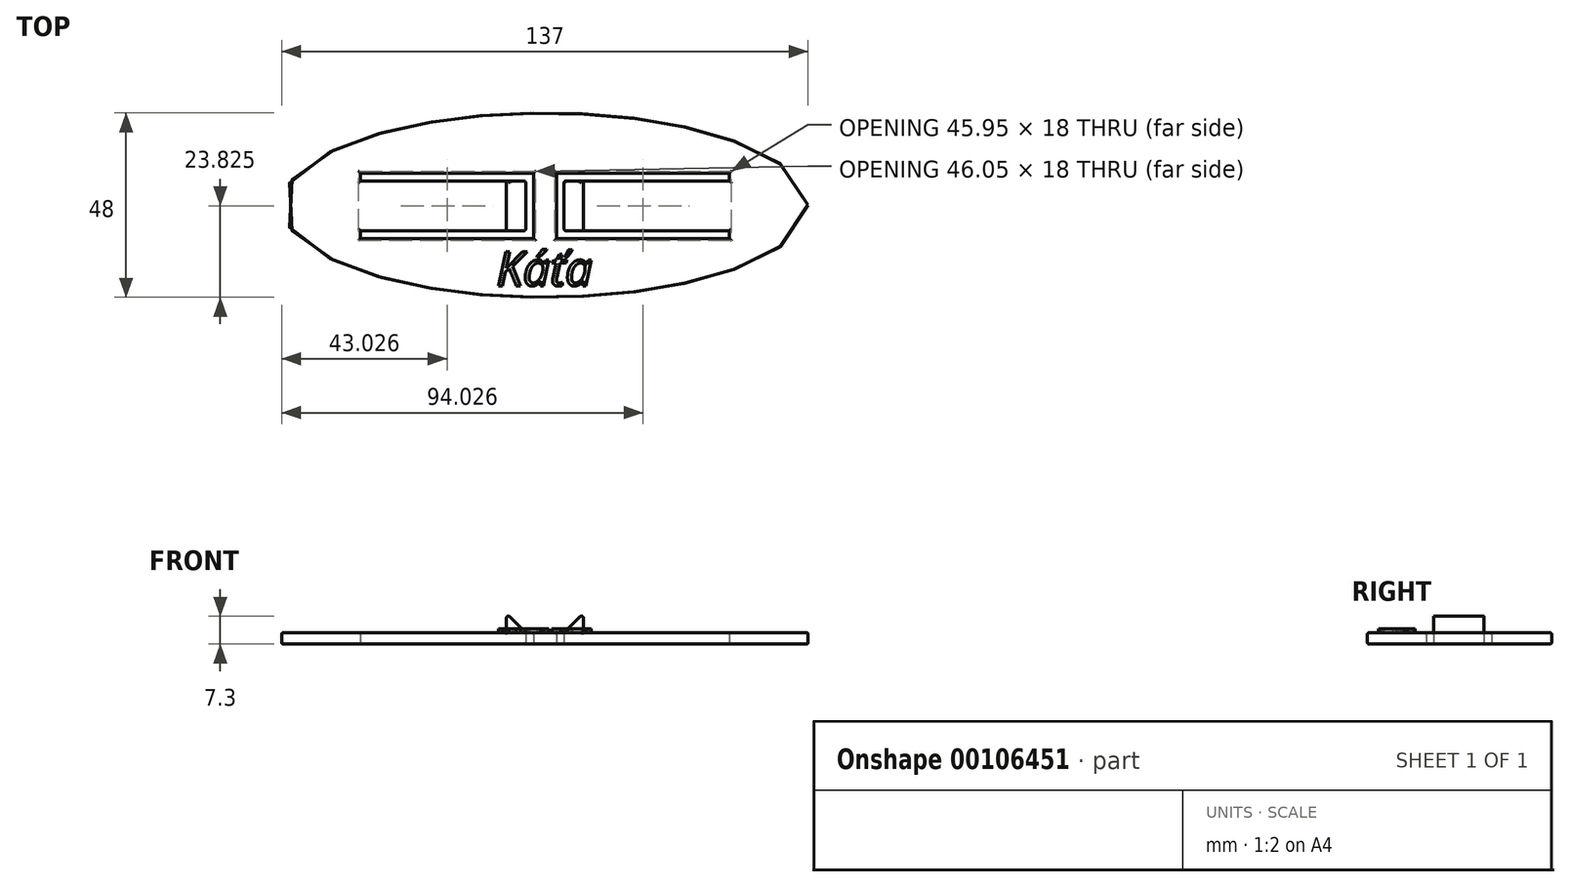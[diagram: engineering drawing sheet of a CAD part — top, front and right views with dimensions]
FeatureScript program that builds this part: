
annotation { "Feature Type Name" : "Feature", "Feature Type Description" : "" }
export const myFeature = defineFeature(function(context is Context, id is Id, definition is map)
    precondition{}
    {
        {
            var Q0;
            Q0=qCreatedBy(makeId("Top.planeOp"),FACE);
            var sketch = newSketch(context, id + "F0", { "sketchPlane" : qUnion([Q0])});
            skEllipse(sketch, "E0", {"center": v(0, 0) * mm, "majorRadius": 68.5 * mm, "minorRadius": 24 * mm, "majorAxis": v(1, 0)});
            skLineSegment(sketch, "E1", {"start": v(-5, -6.67) * mm, "end": v(-48, -6.67) * mm});
            skLineSegment(sketch, "E2", {"start": v(-48, -6.67) * mm, "end": v(-48, -8.67) * mm});
            skLineSegment(sketch, "E3", {"start": v(48, -8.67) * mm, "end": v(48, -6.67) * mm});
            skLineSegment(sketch, "E4", {"start": v(48, -6.67) * mm, "end": v(5, -6.67) * mm});
            skLineSegment(sketch, "E5", {"start": v(5, -6.67) * mm, "end": v(5, 6.33) * mm});
            skLineSegment(sketch, "E6", {"start": v(5, 6.33) * mm, "end": v(48, 6.33) * mm});
            skLineSegment(sketch, "E7", {"start": v(48, 6.33) * mm, "end": v(48, 8.33) * mm});
            skLineSegment(sketch, "E8", {"start": v(-48, 8.33) * mm, "end": v(-48, 6.33) * mm});
            skLineSegment(sketch, "E9", {"start": v(-48, 6.33) * mm, "end": v(-5, 6.33) * mm});
            skLineSegment(sketch, "E10", {"start": v(-5, 6.33) * mm, "end": v(-5, -6.67) * mm});
            skLineSegment(sketch, "E11.left", {"start": v(-2.95, 8.33) * mm, "end": v(-2.95, -8.67) * mm});
            skLineSegment(sketch, "E11.right", {"start": v(3.05, 8.33) * mm, "end": v(3.05, -8.67) * mm});
            skLineSegment(sketch, "E12", {"start": v(-48, -8.67) * mm, "end": v(-2.95, -8.67) * mm});
            skLineSegment(sketch, "E13", {"start": v(3.05, -8.67) * mm, "end": v(48, -8.67) * mm});
            skLineSegment(sketch, "E14", {"start": v(48, 8.33) * mm, "end": v(3.05, 8.33) * mm});
            skLineSegment(sketch, "E15", {"start": v(-2.95, 8.33) * mm, "end": v(-48, 8.33) * mm});
            skLineSegment(sketch, "E16", {"start": v(-70.2, 0) * mm, "end": v(71.44, 0) * mm, "construction": true});
            skPoint(sketch, "E16.endSnap0", {"position": v(68.5, 0) * mm});
            skLineSegment(sketch, "E17", {"start": v(0, -24) * mm, "end": v(71.65, -24) * mm, "construction": true});
            skLineSegment(sketch, "E18", {"start": v(-6.89, -6.67) * mm, "end": v(-6.89, 6.33) * mm, "construction": true});
            skLineSegment(sketch, "E19", {"start": v(7.19, -6.67) * mm, "end": v(7.19, 6.33) * mm, "construction": true});
            skSolve(sketch);
        }
        {
            var Q0;
            Q0=makeQuery(id+"F0.imprint","IMPRINT",FACE,{"disambiguationData":[TD([[makeQuery(id+"F0.imprint","IMPRINT",EDGE,{"derivedFrom":sQuery(id+"F0.wireOp",EDGE,"E0")}),1.0]])]});
            extrude(context, id + "F1", {"entities" : qUnion([Q0]), "endBound" : BoundingType.SYMMETRIC, "depth" : 3 * mm});
        }
        {
            var Q0;
            Q0=makeQuery(id+"F1.opExtrude","CAP_FACE",FACE,{"disambiguationData":[OSD([sQuery(id+"F0.wireOp",EDGE,"E0"),sQuery(id+"F0.wireOp",EDGE,"E1"),sQuery(id+"F0.wireOp",EDGE,"E2"),sQuery(id+"F0.wireOp",EDGE,"E3"),sQuery(id+"F0.wireOp",EDGE,"E4"),sQuery(id+"F0.wireOp",EDGE,"E5"),sQuery(id+"F0.wireOp",EDGE,"E6"),sQuery(id+"F0.wireOp",EDGE,"E7"),sQuery(id+"F0.wireOp",EDGE,"E8"),sQuery(id+"F0.wireOp",EDGE,"E9"),sQuery(id+"F0.wireOp",EDGE,"E10"),sQuery(id+"F0.wireOp",EDGE,"E11.left"),sQuery(id+"F0.wireOp",EDGE,"E11.right"),sQuery(id+"F0.wireOp",EDGE,"E12"),sQuery(id+"F0.wireOp",EDGE,"E13"),sQuery(id+"F0.wireOp",EDGE,"E14"),sQuery(id+"F0.wireOp",EDGE,"E15")])],"isStart":false});
            var sketch = newSketch(context, id + "F2", { "sketchPlane" : qUnion([Q0])});
            skLineSegment(sketch, "E20.bottom", {"start": v(-10, 6.33) * mm, "end": v(-5, 6.33) * mm});
            skLineSegment(sketch, "E20.top", {"start": v(-10, -6.67) * mm, "end": v(-5, -6.67) * mm});
            skLineSegment(sketch, "E20.left", {"start": v(-10, 6.33) * mm, "end": v(-10, -6.67) * mm});
            skLineSegment(sketch, "E20.right", {"start": v(-5, 6.33) * mm, "end": v(-5, -6.67) * mm});
            skLineSegment(sketch, "E21.bottom", {"start": v(5, 6.33) * mm, "end": v(10, 6.33) * mm});
            skLineSegment(sketch, "E21.top", {"start": v(5, -6.67) * mm, "end": v(10, -6.67) * mm});
            skLineSegment(sketch, "E21.left", {"start": v(5, 6.33) * mm, "end": v(5, -6.67) * mm});
            skLineSegment(sketch, "E21.right", {"start": v(10, 6.33) * mm, "end": v(10, -6.67) * mm});
            skSolve(sketch);
        }
        {
            var Q0;
            Q0=makeQuery(id+"F2.imprint","IMPRINT",FACE,{"disambiguationData":[TD([[makeQuery(id+"F2.imprint","IMPRINT",EDGE,{"derivedFrom":sQuery(id+"F2.wireOp",EDGE,"E20.bottom")}),-1.0]])]});
            extrude(context, id + "F3", {"entities" : qUnion([Q0]), "operationType" : NewBodyOperationType.ADD, "depth" : 5 * mm});
        }
        {
            var Q0;
            Q0=makeQuery(id+"F2.imprint","IMPRINT",FACE,{"disambiguationData":[TD([[makeQuery(id+"F2.imprint","IMPRINT",EDGE,{"derivedFrom":sQuery(id+"F2.wireOp",EDGE,"E21.bottom")}),-1.0]])]});
            extrude(context, id + "F4", {"entities" : qUnion([Q0]), "operationType" : NewBodyOperationType.ADD, "depth" : 5 * mm});
        }
        {
            var Q0;
            Q0=makeQuery(id+"F3.boolean.opBoolean","MERGE",FACE,{"derivedFrom":[makeQuery(id+"F1.opExtrude","SWEPT_FACE",FACE,{"disambiguationData":[OSD([sQuery(id+"F0.wireOp",EDGE,"E1")])]}),makeQuery(id+"F3.opExtrude","SWEPT_FACE",FACE,{"disambiguationData":[OSD([sQuery(id+"F2.wireOp",EDGE,"E20.top")])]})]});
            var sketch = newSketch(context, id + "F5", { "sketchPlane" : qUnion([Q0])});
            skLineSegment(sketch, "E22", {"start": v(-5, 1.57) * mm, "end": v(-10, 6.5) * mm});
            skSolve(sketch);
        }
        {
            var Q0;
            {var subQ0=sQuery(id+"F5.wireOp",EDGE,"E22");Q0=makeQuery(id+"F5.imprint","IMPRINT",FACE,{"disambiguationData":[TD([[makeQuery(id+"F5.imprint","IMPRINT",EDGE,{"derivedFrom":subQ0}),-1.0]])]});}
            extrude(context, id + "F6", {"entities" : qUnion([Q0]), "operationType" : NewBodyOperationType.REMOVE, "oppositeDirection" : true, "depth" : 25 * mm});
        }
        {
            var Q0;
            Q0=makeQuery(id+"F4.boolean.opBoolean","MERGE",FACE,{"derivedFrom":[makeQuery(id+"F1.opExtrude","SWEPT_FACE",FACE,{"disambiguationData":[OSD([sQuery(id+"F0.wireOp",EDGE,"E4")])]}),makeQuery(id+"F4.opExtrude","SWEPT_FACE",FACE,{"disambiguationData":[OSD([sQuery(id+"F2.wireOp",EDGE,"E21.top")])]})]});
            var sketch = newSketch(context, id + "F7", { "sketchPlane" : qUnion([Q0])});
            skLineSegment(sketch, "E23", {"start": v(10, 6.5) * mm, "end": v(5, 1.5) * mm});
            skSolve(sketch);
        }
        {
            var Q0;
            {var subQ0=sQuery(id+"F7.wireOp",EDGE,"E23");Q0=makeQuery(id+"F7.imprint","IMPRINT",FACE,{"disambiguationData":[TD([[makeQuery(id+"F7.imprint","IMPRINT",EDGE,{"derivedFrom":subQ0}),-1.0]])]});}
            extrude(context, id + "F8", {"entities" : qUnion([Q0]), "operationType" : NewBodyOperationType.REMOVE, "oppositeDirection" : true, "depth" : 25 * mm});
        }
        {
            var Q0;
            Q0=makeQuery(id+"F1.opExtrude","CAP_EDGE",EDGE,{"disambiguationData":[OSD([sQuery(id+"F0.wireOp",EDGE,"E0")])],"isStart":false});
            var Q1;
            Q1=makeQuery(id+"F1.opExtrude","CAP_EDGE",EDGE,{"disambiguationData":[OSD([sQuery(id+"F0.wireOp",EDGE,"E0")])],"isStart":true});
            var Q2;
            Q2=makeQuery(id+"F1.opExtrude","CAP_EDGE",EDGE,{"disambiguationData":[OSD([sQuery(id+"F0.wireOp",EDGE,"E13")])],"isStart":false});
            var Q3;
            Q3=makeQuery(id+"F1.opExtrude","CAP_EDGE",EDGE,{"disambiguationData":[OSD([sQuery(id+"F0.wireOp",EDGE,"E4")])],"isStart":false});
            var Q4;
            Q4=makeQuery(id+"F1.opExtrude","CAP_EDGE",EDGE,{"disambiguationData":[OSD([sQuery(id+"F0.wireOp",EDGE,"E3")])],"isStart":false});
            var Q5;
            Q5=makeQuery(id+"F8.boolean.opBoolean","COPY",EDGE,{"derivedFrom":makeQuery(id+"F8.opExtrude","CAP_EDGE",EDGE,{"disambiguationData":[OSD([sQuery(id+"F7.wireOp",EDGE,"E23")])],"isStart":true})});
            var Q6;
            Q6=makeQuery(id+"F4.boolean.opBoolean","MERGE",EDGE,{"derivedFrom":[makeQuery(id+"F1.opExtrude","SWEPT_EDGE",EDGE,{"disambiguationData":[OSD([sQuery(id+"F0.wireOp",EDGE,"E4"),sQuery(id+"F0.wireOp",EDGE,"E5")])]}),makeQuery(id+"F4.opExtrude","SWEPT_EDGE",EDGE,{"disambiguationData":[OSD([sQuery(id+"F2.wireOp",EDGE,"E21.top"),sQuery(id+"F2.wireOp",EDGE,"E21.left")])]})]});
            var Q7;
            Q7=makeQuery(id+"F8.boolean.opBoolean","COPY",EDGE,{"derivedFrom":makeQuery(id+"F8.opExtrude","SWEPT_EDGE",EDGE,{"disambiguationData":[OSD([sQuery(id+"F0.wireOp",EDGE,"E4"),sQuery(id+"F0.wireOp",EDGE,"E5"),sQuery(id+"F2.wireOp",EDGE,"E21.top"),sQuery(id+"F2.wireOp",EDGE,"E21.left"),sQuery(id+"F7.wireOp",EDGE,"E23")])]})});
            var Q8;
            Q8=makeQuery(id+"F8.boolean.opBoolean","INTERSECT",EDGE,{"derivedFrom":[makeQuery(id+"F4.boolean.opBoolean","MERGE",FACE,{"derivedFrom":[makeQuery(id+"F1.opExtrude","SWEPT_FACE",FACE,{"disambiguationData":[OSD([sQuery(id+"F0.wireOp",EDGE,"E6")])]}),makeQuery(id+"F4.opExtrude","SWEPT_FACE",FACE,{"disambiguationData":[OSD([sQuery(id+"F2.wireOp",EDGE,"E21.bottom")])]})]}),makeQuery(id+"F8.opExtrude","SWEPT_FACE",FACE,{"disambiguationData":[OSD([sQuery(id+"F7.wireOp",EDGE,"E23")])]})]});
            var Q9;
            Q9=makeQuery(id+"F6.boolean.opBoolean","COPY",EDGE,{"derivedFrom":makeQuery(id+"F6.opExtrude","SWEPT_EDGE",EDGE,{"disambiguationData":[OSD([sQuery(id+"F0.wireOp",EDGE,"E1"),sQuery(id+"F0.wireOp",EDGE,"E10"),sQuery(id+"F2.wireOp",EDGE,"E20.top"),sQuery(id+"F2.wireOp",EDGE,"E20.right"),sQuery(id+"F5.wireOp",EDGE,"E22")])]})});
            var Q10;
            Q10=makeQuery(id+"F6.boolean.opBoolean","INTERSECT",EDGE,{"derivedFrom":[makeQuery(id+"F3.boolean.opBoolean","MERGE",FACE,{"derivedFrom":[makeQuery(id+"F1.opExtrude","SWEPT_FACE",FACE,{"disambiguationData":[OSD([sQuery(id+"F0.wireOp",EDGE,"E9")])]}),makeQuery(id+"F3.opExtrude","SWEPT_FACE",FACE,{"disambiguationData":[OSD([sQuery(id+"F2.wireOp",EDGE,"E20.bottom")])]})]}),makeQuery(id+"F6.opExtrude","SWEPT_FACE",FACE,{"disambiguationData":[OSD([sQuery(id+"F5.wireOp",EDGE,"E22")])]})]});
            var Q11;
            {var subQ0=sQuery(id+"F2.wireOp",EDGE,"E20.left");Q11=makeQuery(id+"F6.boolean.opBoolean","MERGE",EDGE,{"derivedFrom":[makeQuery(id+"F3.opExtrude","CAP_EDGE",EDGE,{"disambiguationData":[OSD([subQ0])],"isStart":false}),makeQuery(id+"F6.opExtrude","SWEPT_EDGE",EDGE,{"disambiguationData":[OSD([sQuery(id+"F0.wireOp",EDGE,"E1"),sQuery(id+"F2.wireOp",EDGE,"E20.top"),subQ0,sQuery(id+"F5.wireOp",EDGE,"E22")])]})]});}
            var Q12;
            Q12=makeQuery(id+"F6.boolean.opBoolean","COPY",EDGE,{"derivedFrom":makeQuery(id+"F6.opExtrude","CAP_EDGE",EDGE,{"disambiguationData":[OSD([sQuery(id+"F5.wireOp",EDGE,"E22")])],"isStart":true})});
            var Q13;
            {var subQ0=sQuery(id+"F2.wireOp",EDGE,"E21.right");Q13=makeQuery(id+"F8.boolean.opBoolean","MERGE",EDGE,{"derivedFrom":[makeQuery(id+"F4.opExtrude","CAP_EDGE",EDGE,{"disambiguationData":[OSD([subQ0])],"isStart":false}),makeQuery(id+"F8.opExtrude","SWEPT_EDGE",EDGE,{"disambiguationData":[OSD([sQuery(id+"F0.wireOp",EDGE,"E4"),sQuery(id+"F2.wireOp",EDGE,"E21.top"),subQ0,sQuery(id+"F7.wireOp",EDGE,"E23")])]})]});}
            var Q14;
            Q14=makeQuery(id+"F1.opExtrude","CAP_EDGE",EDGE,{"disambiguationData":[OSD([sQuery(id+"F0.wireOp",EDGE,"E11.left")])],"isStart":false});
            var Q15;
            Q15=makeQuery(id+"F1.opExtrude","CAP_EDGE",EDGE,{"disambiguationData":[OSD([sQuery(id+"F0.wireOp",EDGE,"E11.right")])],"isStart":false});
            var Q16;
            Q16=makeQuery(id+"F1.opExtrude","CAP_EDGE",EDGE,{"disambiguationData":[OSD([sQuery(id+"F0.wireOp",EDGE,"E14")])],"isStart":false});
            var Q17;
            Q17=makeQuery(id+"F1.opExtrude","CAP_EDGE",EDGE,{"disambiguationData":[OSD([sQuery(id+"F0.wireOp",EDGE,"E6")])],"isStart":false});
            var Q18;
            Q18=makeQuery(id+"F1.opExtrude","CAP_EDGE",EDGE,{"disambiguationData":[OSD([sQuery(id+"F0.wireOp",EDGE,"E7")])],"isStart":false});
            var Q19;
            Q19=makeQuery(id+"F1.opExtrude","CAP_EDGE",EDGE,{"disambiguationData":[OSD([sQuery(id+"F0.wireOp",EDGE,"E15")])],"isStart":false});
            var Q20;
            Q20=makeQuery(id+"F1.opExtrude","CAP_EDGE",EDGE,{"disambiguationData":[OSD([sQuery(id+"F0.wireOp",EDGE,"E9")])],"isStart":false});
            var Q21;
            Q21=makeQuery(id+"F1.opExtrude","CAP_EDGE",EDGE,{"disambiguationData":[OSD([sQuery(id+"F0.wireOp",EDGE,"E1")])],"isStart":false});
            var Q22;
            Q22=makeQuery(id+"F1.opExtrude","CAP_EDGE",EDGE,{"disambiguationData":[OSD([sQuery(id+"F0.wireOp",EDGE,"E12")])],"isStart":false});
            var Q23;
            Q23=makeQuery(id+"F1.opExtrude","CAP_EDGE",EDGE,{"disambiguationData":[OSD([sQuery(id+"F0.wireOp",EDGE,"E2")])],"isStart":false});
            var Q24;
            Q24=makeQuery(id+"F1.opExtrude","CAP_EDGE",EDGE,{"disambiguationData":[OSD([sQuery(id+"F0.wireOp",EDGE,"E8")])],"isStart":false});
            var Q25;
            Q25=makeQuery(id+"F1.opExtrude","CAP_EDGE",EDGE,{"disambiguationData":[OSD([sQuery(id+"F0.wireOp",EDGE,"E15")])],"isStart":true});
            var Q26;
            Q26=makeQuery(id+"F1.opExtrude","CAP_EDGE",EDGE,{"disambiguationData":[OSD([sQuery(id+"F0.wireOp",EDGE,"E11.left")])],"isStart":true});
            var Q27;
            Q27=makeQuery(id+"F3.boolean.opBoolean","MERGE",EDGE,{"derivedFrom":[makeQuery(id+"F1.opExtrude","SWEPT_EDGE",EDGE,{"disambiguationData":[OSD([sQuery(id+"F0.wireOp",EDGE,"E9"),sQuery(id+"F0.wireOp",EDGE,"E10")])]}),makeQuery(id+"F3.opExtrude","SWEPT_EDGE",EDGE,{"disambiguationData":[OSD([sQuery(id+"F2.wireOp",EDGE,"E20.bottom"),sQuery(id+"F2.wireOp",EDGE,"E20.right")])]})]});
            var Q28;
            Q28=makeQuery(id+"F1.opExtrude","CAP_EDGE",EDGE,{"disambiguationData":[OSD([sQuery(id+"F0.wireOp",EDGE,"E8")])],"isStart":true});
            var Q29;
            Q29=makeQuery(id+"F1.opExtrude","CAP_EDGE",EDGE,{"disambiguationData":[OSD([sQuery(id+"F0.wireOp",EDGE,"E9")])],"isStart":true});
            var Q30;
            Q30=makeQuery(id+"F1.opExtrude","CAP_EDGE",EDGE,{"disambiguationData":[OSD([sQuery(id+"F0.wireOp",EDGE,"E2")])],"isStart":true});
            var Q31;
            Q31=makeQuery(id+"F1.opExtrude","CAP_EDGE",EDGE,{"disambiguationData":[OSD([sQuery(id+"F0.wireOp",EDGE,"E12")])],"isStart":true});
            var Q32;
            Q32=makeQuery(id+"F1.opExtrude","CAP_EDGE",EDGE,{"disambiguationData":[OSD([sQuery(id+"F0.wireOp",EDGE,"E10")])],"isStart":true});
            var Q33;
            Q33=makeQuery(id+"F1.opExtrude","CAP_FACE",FACE,{"disambiguationData":[OSD([sQuery(id+"F0.wireOp",EDGE,"E0"),sQuery(id+"F0.wireOp",EDGE,"E1"),sQuery(id+"F0.wireOp",EDGE,"E2"),sQuery(id+"F0.wireOp",EDGE,"E3"),sQuery(id+"F0.wireOp",EDGE,"E4"),sQuery(id+"F0.wireOp",EDGE,"E5"),sQuery(id+"F0.wireOp",EDGE,"E6"),sQuery(id+"F0.wireOp",EDGE,"E7"),sQuery(id+"F0.wireOp",EDGE,"E8"),sQuery(id+"F0.wireOp",EDGE,"E9"),sQuery(id+"F0.wireOp",EDGE,"E10"),sQuery(id+"F0.wireOp",EDGE,"E11.left"),sQuery(id+"F0.wireOp",EDGE,"E11.right"),sQuery(id+"F0.wireOp",EDGE,"E12"),sQuery(id+"F0.wireOp",EDGE,"E13"),sQuery(id+"F0.wireOp",EDGE,"E14"),sQuery(id+"F0.wireOp",EDGE,"E15")])],"isStart":true});
            fillet(context, id + "F9", {"entities" : qUnion([Q0, Q1, Q2, Q3, Q4, Q5, Q6, Q7, Q8, Q9, Q10, Q11, Q12, Q13, Q14, Q15, Q16, Q17, Q18, Q19, Q20, Q21, Q22, Q23, Q24, Q25, Q26, Q27, Q28, Q29, Q30, Q31, Q32, Q33]), "radius" : 0.5 * mm, "allowEdgeOverflow" : false});
        }
        {
            var Q0;
            Q0=makeQuery(id+"F3.boolean.opBoolean","MERGE",EDGE,{"derivedFrom":[makeQuery(id+"F1.opExtrude","SWEPT_EDGE",EDGE,{"disambiguationData":[OSD([sQuery(id+"F0.wireOp",EDGE,"E1"),sQuery(id+"F0.wireOp",EDGE,"E10")])]}),makeQuery(id+"F3.opExtrude","SWEPT_EDGE",EDGE,{"disambiguationData":[OSD([sQuery(id+"F2.wireOp",EDGE,"E20.top"),sQuery(id+"F2.wireOp",EDGE,"E20.right")])]})]});
            var Q1;
            Q1=makeQuery(id+"F9.opFillet","BLEND_EDGE",EDGE,{"blendedFrom":[makeQuery(id+"F1.opExtrude","CAP_EDGE",EDGE,{"disambiguationData":[OSD([sQuery(id+"F0.wireOp",EDGE,"E5")])],"isStart":true}),makeQuery(id+"F1.opExtrude","CAP_EDGE",EDGE,{"disambiguationData":[OSD([sQuery(id+"F0.wireOp",EDGE,"E6")])],"isStart":true})],"blendedInto":[]});
            fillet(context, id + "F10", {"entities" : qUnion([Q0, Q1]), "radius" : 0.5 * mm, "tangentPropagation" : true, "allowEdgeOverflow" : false});
        }
        {
            var Q0;
            {var subQ4=sQuery(id+"F2.wireOp",EDGE,"E20.left");Q0=makeQuery(id+"F2.imprint","IMPRINT",FACE,{"disambiguationData":[TD([[makeQuery(id+"F2.imprint","IMPRINT",EDGE,{"derivedFrom":subQ4}),-1.0]])]});}
            var sketch = newSketch(context, id + "F11", { "sketchPlane" : qUnion([Q0])});
            skText(sketch, "E24", { "text": "Káťa\n", "fontName": "OpenSans-Italic.ttf"});
            const initialGuessF11  = {"E24": [-0.01259, -0.02097, 1, 0, 0.0089]};
            skSetInitialGuess(sketch, initialGuessF11);
            skSolve(sketch);
        }
        {
            var Q0;
            Q0=qSketchRegion(id+"F11",true);
            extrude(context, id + "F12", {"entities" : qUnion([Q0]), "operationType" : NewBodyOperationType.ADD, "depth" : 1 * mm});
        }
    });
